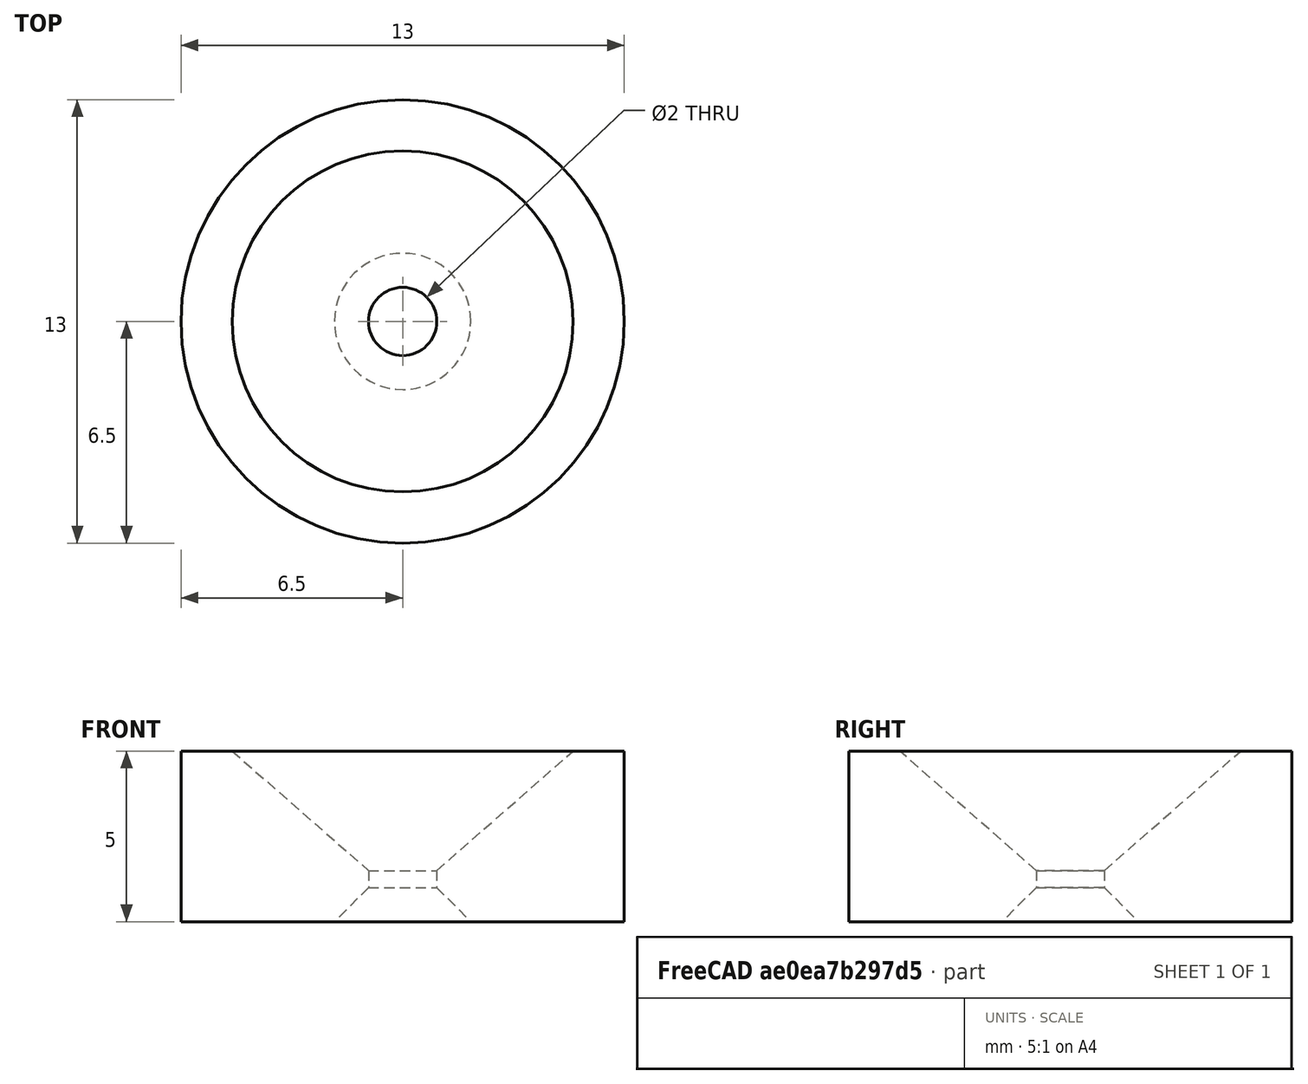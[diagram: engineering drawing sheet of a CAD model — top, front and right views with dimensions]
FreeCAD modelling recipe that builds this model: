
FCSTD DOCUMENT  (FreeCAD 0.18.4R)
Label: nozzle_big
Comment: # 2020-02-12 13:39:12: read from <userpath>/repositories/sussex_neuro/Olfactometer/hardware/mechanics/from_raiser_et_al/nozzle_big.ipt
License: All rights reserved
LicenseURL: http://en.wikipedia.org/wiki/All_rights_reserved
objects: Sketcher::SketchObject×2, Spreadsheet::Sheet×1, Part::Revolution×1
note: 3 computed .brp shape members not serialized (recipe doc carries the construction recipe); baked Part::Feature solids carry a one-line shape summary decoded from their .brp

FEATURE [Spreadsheet::Sheet] Parameters
  cells = A1=Parameter; B1=Value; C1=Fromula; D1=Tolerance; E1=Comment; A2=d11; B2(d11_)=6.5; C2=6.5mm; D2=NOMINAL; A3=d13; B3(d13_)=90; C3=90°; D3=NOMINAL; A4=d19; B4(d19_)=0.5; C4=0.5mm; D4=NOMINAL; A5=d20; B5(d20_)=2; C5=2mm; D5=NOMINAL; A6=d21; B6(d21_)=0; C6=0mm; D6=NOMINAL; A7=d22; B7(d22_)=20; C7=20mm; D7=NOMINAL; A8=d26; B8(d26_)=4.5; C8=4.5mm; D8=NOMINAL; A9=d27; B9(d27_)=0.5; C9=0.5mm; D9=NOMINAL; A10=d28; B10(d28_)=1; C10=1mm; D10=NOMINAL; A11=d29; B11(d29_)=2; C11=2mm; D11=NOMINAL; A12=d30; B12(d30_)=0.2; C12=0.2mm; D12=NOMINAL; A13=d31; B13(d31_)=1; C13=1mm; D13=NOMINAL; A14=d32; B14(d32_)=0.5; C14=0.5mm; D14=NOMINAL; A15=d33; B15(d33_)=2; C15=2mm; D15=NOMINAL; A16=d34; B16(d34_)=0; C16=0mm; D16=NOMINAL; A17=d35; B17(d35_)=20; C17=20mm; D17=NOMINAL; A18=d36; B18(d36_)=0.5; C18=0.5mm; D18=NOMINAL; A19=d37; B19(d37_)=2; C19=2mm; D19=NOMINAL; A20=d38; B20(d38_)=0; C20=0mm; D20=NOMINAL; A21=d39; B21(d39_)=20; C21=20mm; D21=NOMINAL; A22=d4; B22(d4_)=5; C22=5mm; D22=NOMINAL; A23=d5; B23(d5_)=1.5; C23=1.5mm; D23=NOMINAL
FEATURE [Sketcher::SketchObject] Sketch2
  Placement = pos=(0,0,0) rot=(0,0.707107,0.707107;3.14159rad)
  sketch-geometry (8):
    g0: LineSegment StartX=6.5 StartY=8e-16 StartZ=0 EndX=6.5 EndY=5 EndZ=0
    g1: LineSegment StartX=6.5 StartY=5 StartZ=0 EndX=5 EndY=5 EndZ=0
    g2: LineSegment StartX=6.5 StartY=5 StartZ=0 EndX=6.5 EndY=9e-16 EndZ=0
    g3: LineSegment [constr] StartX=0 StartY=-1 StartZ=0 EndX=0 EndY=6 EndZ=0
    g4: LineSegment StartX=6.5 StartY=8e-16 StartZ=0 EndX=2 EndY=8e-16 EndZ=0
    g5: LineSegment StartX=2 StartY=8e-16 StartZ=0 EndX=1 EndY=1 EndZ=0
    g6: LineSegment StartX=1 StartY=1 StartZ=0 EndX=1 EndY=1.5 EndZ=0
    g7: LineSegment StartX=5 StartY=5 StartZ=0 EndX=1 EndY=1.5 EndZ=0
  constraints (7):
    c: Perpendicular(g1,g0)
    c: Perpendicular(g3,g4)
    c: Perpendicular(g4,g6)
    c: Coincident(g0,g2)
    c: Coincident(g0,g4)
    c: Coincident(g0,g1)
    c: Coincident(g0,g2)
FEATURE [Sketcher::SketchObject] Sketch2_bp
  Placement = pos=(0,0,0) rot=(0,0.707107,0.707107;3.14159rad)
  sketch-geometry (6):
    g0: LineSegment StartX=6.5 StartY=8e-16 StartZ=0 EndX=6.5 EndY=5 EndZ=0
    g1: LineSegment StartX=6.5 StartY=5 StartZ=0 EndX=5 EndY=5 EndZ=0
    g2: LineSegment StartX=5 StartY=5 StartZ=0 EndX=1 EndY=1.5 EndZ=0
    g3: LineSegment StartX=1 StartY=1.5 StartZ=0 EndX=1 EndY=1 EndZ=0
    g4: LineSegment StartX=1 StartY=1 StartZ=0 EndX=2 EndY=8e-16 EndZ=0
    g5: LineSegment StartX=2 StartY=8e-16 StartZ=0 EndX=6.5 EndY=8e-16 EndZ=0
FEATURE [Part::Revolution] Revolution2
  Angle = 360
  Axis = (0,0,1)
  Base = (0,0,-10)
  FaceMakerClass = Part::FaceMakerBullseye
  Solid = true
  Source = -> Sketch2_bp
  Symmetric = false
